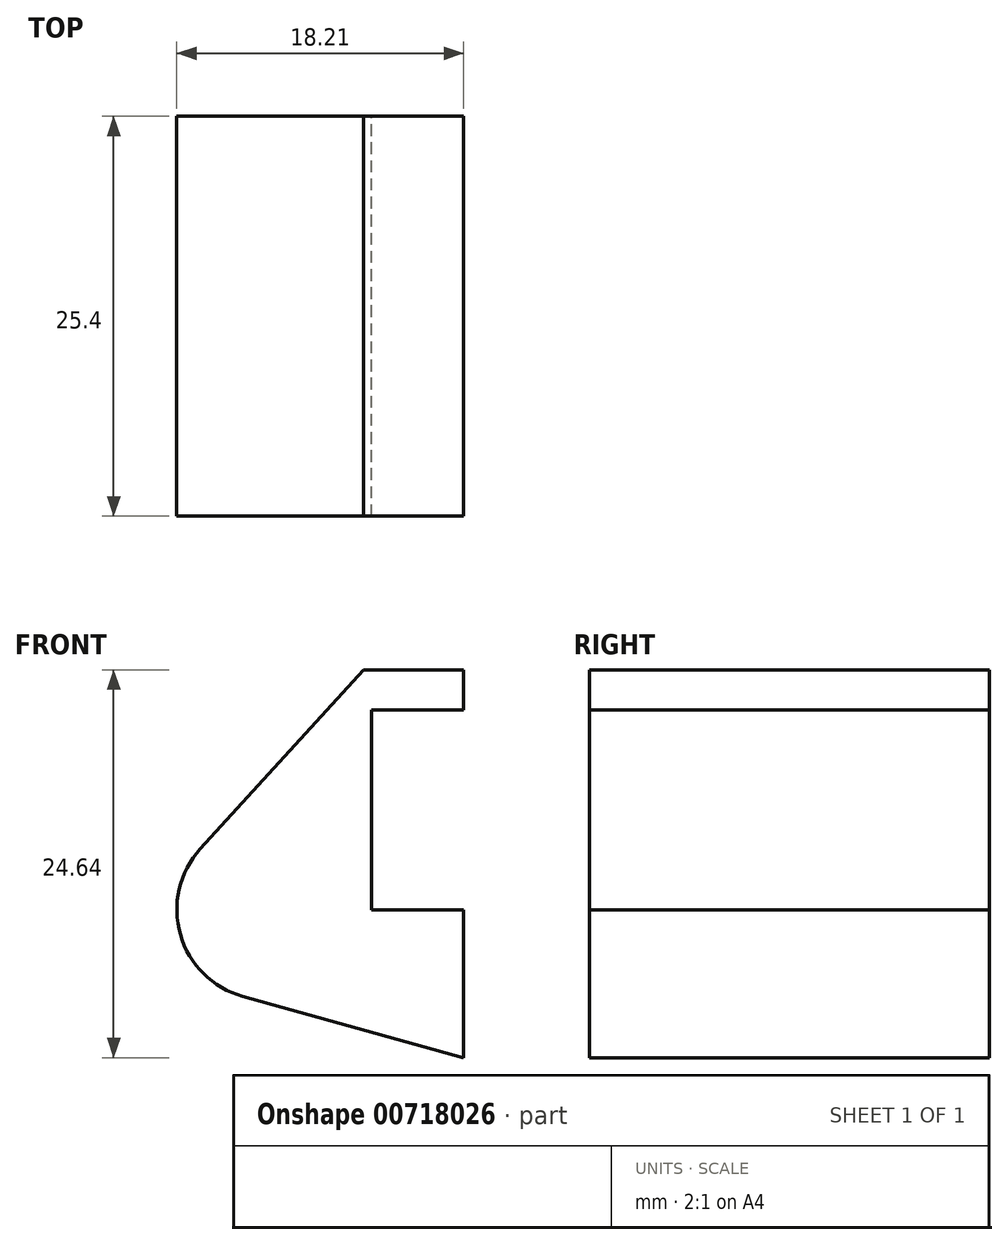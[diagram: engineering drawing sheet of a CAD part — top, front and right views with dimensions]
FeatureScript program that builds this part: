
annotation { "Feature Type Name" : "Feature", "Feature Type Description" : "" }
export const myFeature = defineFeature(function(context is Context, id is Id, definition is map)
    precondition{}
    {
        {
            var Q0;
            Q0=qCreatedBy(makeId("Front.planeOp"),FACE);
            var sketch = newSketch(context, id + "F0", { "sketchPlane" : qUnion([Q0])});
            skLineSegment(sketch, "E0", {"start": v(0, 0) * mm, "end": v(0, 12.7) * mm});
            skLineSegment(sketch, "E1", {"start": v(0, 12.7) * mm, "end": v(10.16, 12.7) * mm});
            skLineSegment(sketch, "E2", {"start": v(10.16, 12.7) * mm, "end": v(10.16, 10.16) * mm});
            skLineSegment(sketch, "E3", {"start": v(10.16, 10.16) * mm, "end": v(56.13, 10.16) * mm});
            skLineSegment(sketch, "E4", {"start": v(56.13, 10.16) * mm, "end": v(56.13, 12.7) * mm});
            skLineSegment(sketch, "E5", {"start": v(56.13, 12.7) * mm, "end": v(66.3, 12.7) * mm});
            skLineSegment(sketch, "E6", {"start": v(66.3, 12.7) * mm, "end": v(66.3, 0) * mm});
            skLineSegment(sketch, "E7", {"start": v(66.3, 0) * mm, "end": v(0, 0) * mm});
            skLineSegment(sketch, "E8", {"start": v(5.84, 15.24) * mm, "end": v(-0.5, 15.24) * mm});
            skLineSegment(sketch, "E9", {"start": v(-0.5, 15.24) * mm, "end": v(-10.88, 3.85) * mm});
            skLineSegment(sketch, "E10", {"start": v(0, 0) * mm, "end": v(-6.65, 0) * mm});
            skCircle(sketch, "E11", {"center": v(-6.65, 0) * mm, "radius": 5.72 * mm});
            skCircle(sketch, "E12", {"center": v(-6.65, 0) * mm, "radius": 3.18 * mm});
            skLineSegment(sketch, "E13", {"start": v(5.84, 15.24) * mm, "end": v(5.84, -9.4) * mm});
            skLineSegment(sketch, "E14", {"start": v(5.84, -9.4) * mm, "end": v(-8.18, -5.5) * mm});
            skSolve(sketch);
        }
        {
            var Q0;
            {var subQ1=sQuery(id+"F0.wireOp",EDGE,"E0");Q0=makeQuery(id+"F0.imprint","IMPRINT",FACE,{"disambiguationData":[TD([[makeQuery(id+"F0.imprint","IMPRINT",EDGE,{"derivedFrom":subQ1}),1.0]])]});}
            var Q1;
            {var subQ5=sQuery(id+"F0.wireOp",EDGE,"E12");Q1=makeQuery(id+"F0.imprint","IMPRINT",FACE,{"disambiguationData":[TD([[makeQuery(id+"F0.imprint","IMPRINT",EDGE,{"derivedFrom":subQ5}),-1.0]])]});}
            var Q2;
            {var subQ0=sQuery(id+"F0.wireOp",EDGE,"E12");Q2=makeQuery(id+"F0.imprint","IMPRINT",FACE,{"disambiguationData":[TD([[makeQuery(id+"F0.imprint","IMPRINT",EDGE,{"derivedFrom":subQ0}),1.0]])]});}
            var Q3;
            {var subQ0=sQuery(id+"F0.wireOp",EDGE,"E14");Q3=makeQuery(id+"F0.imprint","IMPRINT",FACE,{"disambiguationData":[TD([[makeQuery(id+"F0.imprint","IMPRINT",EDGE,{"derivedFrom":subQ0}),-1.0]])]});}
            extrude(context, id + "F1", {"entities" : qUnion([Q0, Q1, Q2, Q3]), "depth" : 25.4 * mm, "offsetDistance" : 25.4 * mm});
        }
    });
